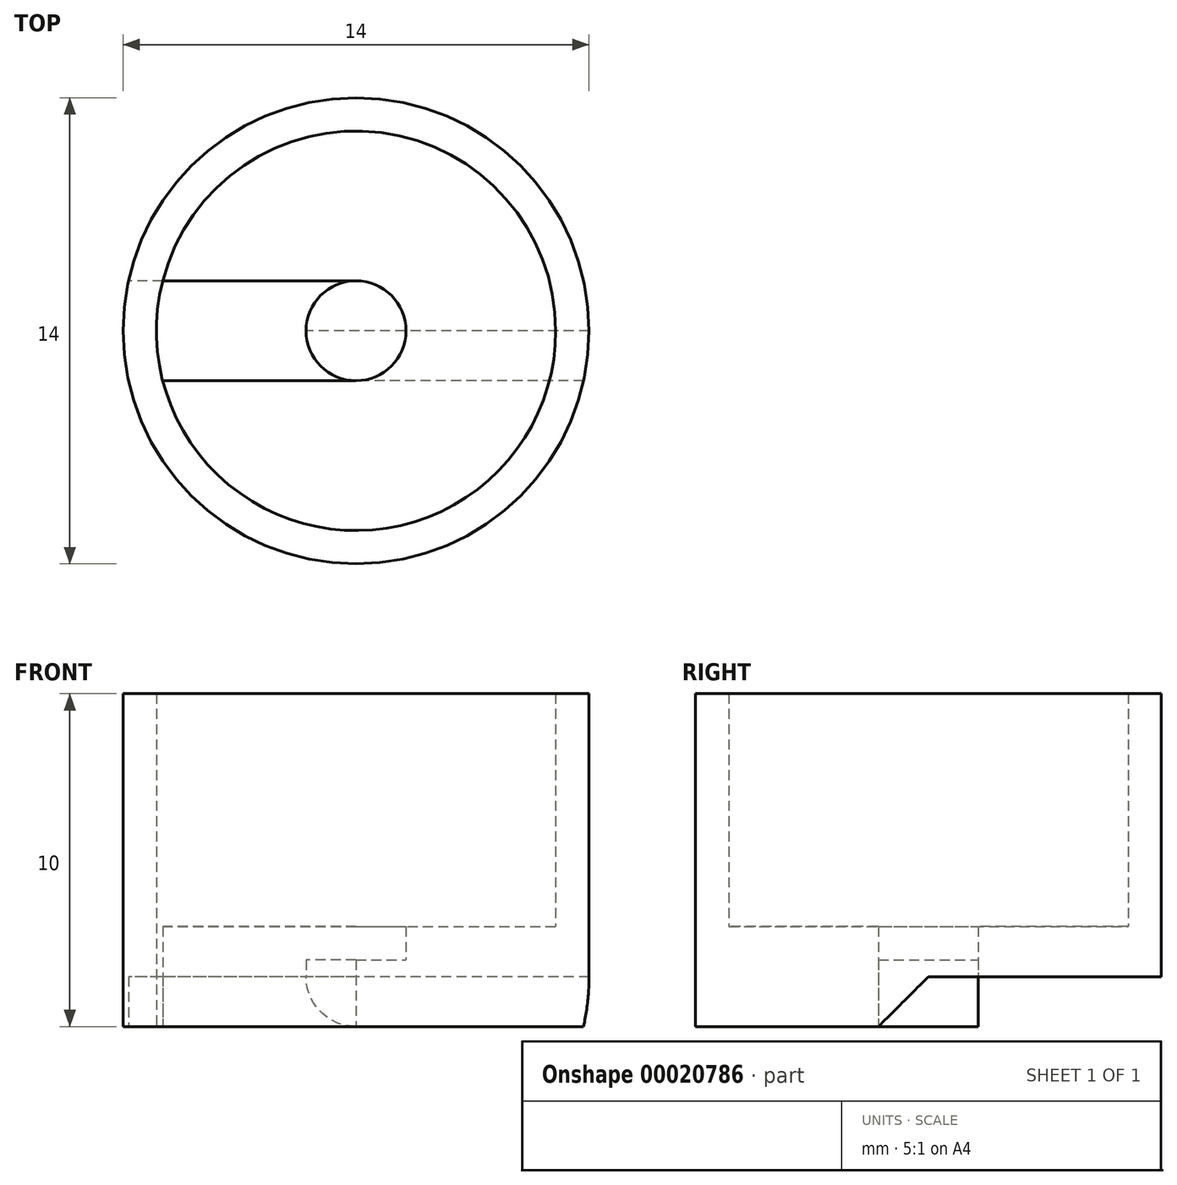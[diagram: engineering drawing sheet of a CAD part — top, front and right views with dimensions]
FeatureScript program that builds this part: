
annotation { "Feature Type Name" : "Feature", "Feature Type Description" : "" }
export const myFeature = defineFeature(function(context is Context, id is Id, definition is map)
    precondition{}
    {
        {
            var Q0;
            Q0=qCreatedBy(makeId("Top.planeOp"),FACE);
            var sketch = newSketch(context, id + "F0", { "sketchPlane" : qUnion([Q0])});
            skCircle(sketch, "E0", {"center": v(0, 0) * mm, "radius": 6 * mm});
            skCircle(sketch, "E1", {"center": v(0, 0) * mm, "radius": 7 * mm});
            skCircle(sketch, "E2", {"center": v(0, 0) * mm, "radius": 1.5 * mm});
            skLineSegment(sketch, "E3", {"start": v(0, 1.5) * mm, "end": v(-6.84, 1.5) * mm});
            skLineSegment(sketch, "E4", {"start": v(-6.84, 1.5) * mm, "end": v(6.84, 1.5) * mm});
            skLineSegment(sketch, "E5", {"start": v(0, -1.5) * mm, "end": v(-6.84, -1.5) * mm});
            skLineSegment(sketch, "E6", {"start": v(-6.84, -1.5) * mm, "end": v(6.84, -1.5) * mm});
            skSolve(sketch);
        }
        {
            var Q0;
            Q0=makeQuery(id+"F0.imprint","IMPRINT",FACE,{"disambiguationData":[TD([[makeQuery(id+"F0.imprint","IMPRINT",EDGE,{"derivedFrom":sQuery(id+"F0.wireOp",EDGE,"E0")}),1.0]])]});
            var Q1;
            {var subQ0=sQuery(id+"F0.wireOp",EDGE,"E4");var subQ3=sQuery(id+"F0.wireOp",EDGE,"E0");var subQ4=makeQuery(id+"F0.imprint","INTERSECT",VERTEX,{"disambiguationData":[OD(0.0)],"derivedFrom":[subQ3,subQ0]});Q1=makeQuery(id+"F0.imprint","IMPRINT",FACE,{"disambiguationData":[TD([[makeQuery(id+"F0.imprint","IMPRINT",EDGE,{"disambiguationData":[TD([[subQ4,-1.0]])],"derivedFrom":subQ3}),1.0]])]});}
            var Q2;
            {var subQ3=sQuery(id+"F0.wireOp",EDGE,"E0");var subQ5=sQuery(id+"F0.wireOp",EDGE,"E4");var subQ7=makeQuery(id+"F0.imprint","INTERSECT",VERTEX,{"disambiguationData":[OD(1.0)],"derivedFrom":[subQ3,subQ5]});Q2=makeQuery(id+"F0.imprint","IMPRINT",FACE,{"disambiguationData":[TD([[makeQuery(id+"F0.imprint","IMPRINT",EDGE,{"disambiguationData":[TD([[subQ7,1.0]])],"derivedFrom":subQ3}),1.0]])]});}
            var Q3;
            Q3=sQuery(id+"F0.wireOp",EDGE,"E0");
            extrude(context, id + "F1", {"entities" : qUnion([Q0, Q1, Q2]), "surfaceEntities" : qUnion([Q3]), "depth" : 3 * mm});
        }
        {
            var Q0;
            Q0 = qSketchRegion(id + "F0", true);
            extrude(context, id + "F2", {"entities" : qUnion([Q0]), "operationType" : NewBodyOperationType.ADD, "depth" : 10 * mm});
        }
        {
            var Q0;
            Q0=makeQuery(id+"F0.imprint","IMPRINT",FACE,{"disambiguationData":[TD([[makeQuery(id+"F0.imprint","IMPRINT",EDGE,{"derivedFrom":sQuery(id+"F0.wireOp",EDGE,"E2")}),1.0]])]});
            extrude(context, id + "F3", {"entities" : qUnion([Q0]), "operationType" : NewBodyOperationType.ADD, "depth" : 2 * mm});
        }
        {
            var Q0;
            {var subQ0=sQuery(id+"F0.wireOp",EDGE,"E4");var subQ3=sQuery(id+"F0.wireOp",EDGE,"E0");var subQ4=makeQuery(id+"F0.imprint","INTERSECT",VERTEX,{"disambiguationData":[OD(0.0)],"derivedFrom":[subQ3,subQ0]});Q0=makeQuery(id+"F0.imprint","IMPRINT",FACE,{"disambiguationData":[TD([[makeQuery(id+"F0.imprint","IMPRINT",EDGE,{"disambiguationData":[TD([[subQ4,-1.0]])],"derivedFrom":subQ3}),1.0]])]});}
            var Q1;
            {var subQ1=sQuery(id+"F0.wireOp",EDGE,"E0");var subQ5=sQuery(id+"F0.wireOp",EDGE,"E4");var subQ6=makeQuery(id+"F0.imprint","INTERSECT",VERTEX,{"disambiguationData":[OD(0.0)],"derivedFrom":[subQ1,subQ5]});Q1=makeQuery(id+"F0.imprint","IMPRINT",FACE,{"disambiguationData":[TD([[makeQuery(id+"F0.imprint","IMPRINT",EDGE,{"disambiguationData":[TD([[subQ6,-1.0]])],"derivedFrom":subQ1}),-1.0]])]});}
            var Q2;
            {var subQ3=sQuery(id+"F0.wireOp",EDGE,"E0");var subQ5=sQuery(id+"F0.wireOp",EDGE,"E4");var subQ7=makeQuery(id+"F0.imprint","INTERSECT",VERTEX,{"disambiguationData":[OD(1.0)],"derivedFrom":[subQ3,subQ5]});Q2=makeQuery(id+"F0.imprint","IMPRINT",FACE,{"disambiguationData":[TD([[makeQuery(id+"F0.imprint","IMPRINT",EDGE,{"disambiguationData":[TD([[subQ7,1.0]])],"derivedFrom":subQ3}),1.0]])]});}
            var Q3;
            {var subQ1=sQuery(id+"F0.wireOp",EDGE,"E0");var subQ5=sQuery(id+"F0.wireOp",EDGE,"E4");var subQ6=makeQuery(id+"F0.imprint","INTERSECT",VERTEX,{"disambiguationData":[OD(1.0)],"derivedFrom":[subQ1,subQ5]});Q3=makeQuery(id+"F0.imprint","IMPRINT",FACE,{"disambiguationData":[TD([[makeQuery(id+"F0.imprint","IMPRINT",EDGE,{"disambiguationData":[TD([[subQ6,1.0]])],"derivedFrom":subQ1}),-1.0]])]});}
            var Q4;
            {var subQ0=sQuery(id+"F0.wireOp",EDGE,"E2");var subQ2=makeQuery(id+"F0.imprint","INTERSECT",VERTEX,{"derivedFrom":[subQ0,sQuery(id+"F0.wireOp",EDGE,"E4")]});Q4=makeQuery(id+"F0.imprint","IMPRINT",FACE,{"disambiguationData":[TD([[makeQuery(id+"F0.imprint","IMPRINT",EDGE,{"disambiguationData":[TD([[subQ2,-1.0]])],"derivedFrom":subQ0}),1.0]])]});}
            extrude(context, id + "F4", {"entities" : qUnion([Q0, Q1, Q2, Q3, Q4]), "operationType" : NewBodyOperationType.REMOVE, "depth" : 1.5 * mm});
        }
        {
            var Q0;
            Q0=makeQuery(id+"F4.boolean.opBoolean","COPY",EDGE,{"derivedFrom":makeQuery(id+"F4.opExtrude","CAP_EDGE",EDGE,{"disambiguationData":[OSD([sQuery(id+"F0.wireOp",EDGE,"E4")])],"isStart":false})});
            var Q1;
            Q1=makeQuery(id+"F4.boolean.opBoolean","COPY",EDGE,{"derivedFrom":makeQuery(id+"F4.opExtrude","CAP_EDGE",EDGE,{"disambiguationData":[OSD([sQuery(id+"F0.wireOp",EDGE,"E6")])],"isStart":false})});
            chamfer(context, id + "F5", {"entities" : qUnion([Q0, Q1]), "width" : 1.5 * mm, "tangentPropagation" : true});
        }
    });
